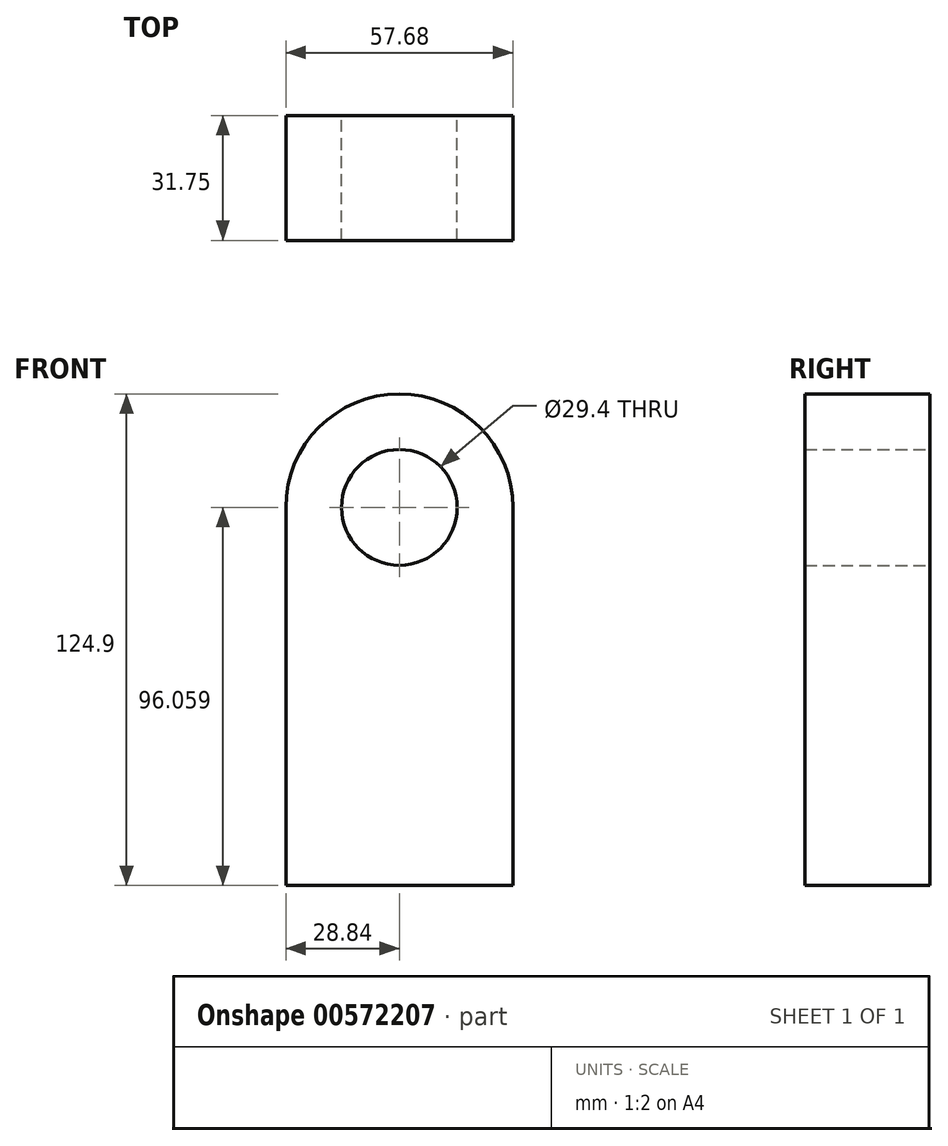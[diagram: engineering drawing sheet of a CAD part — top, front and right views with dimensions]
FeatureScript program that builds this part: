
annotation { "Feature Type Name" : "Feature", "Feature Type Description" : "" }
export const myFeature = defineFeature(function(context is Context, id is Id, definition is map)
    precondition{}
    {
        {
            var Q0;
            Q0=qCreatedBy(makeId("Front.planeOp"),FACE);
            var sketch = newSketch(context, id + "F0", { "sketchPlane" : qUnion([Q0])});
            skLineSegment(sketch, "E0.top", {"start": v(28.84, -48.03) * mm, "end": v(-28.84, -48.03) * mm});
            skLineSegment(sketch, "E0.left", {"start": v(28.84, 48.03) * mm, "end": v(28.84, -48.03) * mm});
            skLineSegment(sketch, "E0.right", {"start": v(-28.84, 48.03) * mm, "end": v(-28.84, -48.03) * mm});
            skPoint(sketch, "E0.middle", {"position": v(0, 0) * mm});
            skCircle(sketch, "E1", {"center": v(0, 48.03) * mm, "radius": 14.7 * mm});
            skArc(sketch, "E2", {"start": v(-28.84, 48.03) * mm, "mid": v(0, 76.87) * mm, "end": v(28.84, 48.03) * mm});
            skSolve(sketch);
        }
        {
            var Q0;
            Q0=makeQuery(id+"F0.imprint","IMPRINT",FACE,{"disambiguationData":[TD([[makeQuery(id+"F0.imprint","IMPRINT",EDGE,{"derivedFrom":sQuery(id+"F0.wireOp",EDGE,"E0.top")}),-1.0]])]});
            extrude(context, id + "F1", {"entities" : qUnion([Q0]), "depth" : 31.75 * mm, "offsetDistance" : 25.4 * mm});
        }
    });
